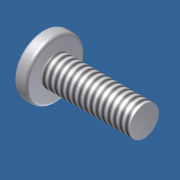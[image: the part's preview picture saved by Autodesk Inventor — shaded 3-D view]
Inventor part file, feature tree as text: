
AUTODESK INVENTOR PART (.ipt)
format: ipt  version: 2012 (Build 160160000, 160)  size: 132,608 bytes
history: native  units: in
note: dims shown in document units (in); Inventor stores cm internally (conversion verified against a paired STEP export)
features: sketch x2, revolve x1, thread x1, extrude x1
ambient origin geometry x8: Origin, YZ Plane, XZ Plane, XY Plane, X Axis, Y Axis, Z Axis, Center Point
bodies: Solid1 (feature_tree)
feature tree (5):
  revolve  "Revolution1"  [1 undecoded]
  thread  "Thread1"  [1 undecoded]
  extrude  "Extrusion1"  TaperAngle=90.0deg  [1 undecoded]
  sketch  "Sketch1"  dims[d1=0.125in d3=0.75in d6=0.5in]
  sketch  "Sketch2"  dims[d8=0.025in d9=90.0deg d10=1.0in d11=0.0in d12=0.035in d13=0.035in d18=0.175in d19=0.0in d20=0.09in d21=0.09in d22=0.09in d23=0.09in]
note: 3 required parameter values undecoded (feature->parameter linkage not recoverable at this tier; creation-order binding heuristic only, values carry confidence <= 0.55)